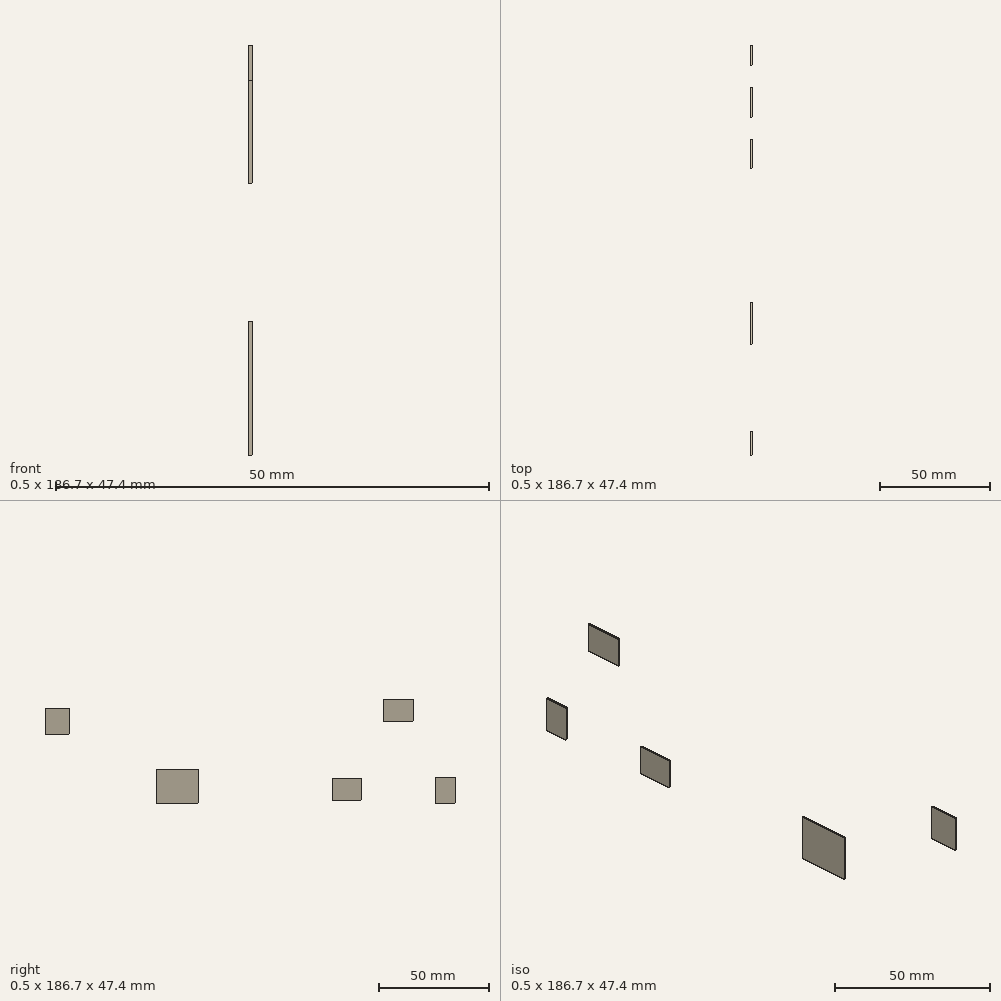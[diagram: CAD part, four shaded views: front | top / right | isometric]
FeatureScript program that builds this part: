
annotation { "Feature Type Name" : "Feature", "Feature Type Description" : "" }
export const myFeature = defineFeature(function(context is Context, id is Id, definition is map)
    precondition{}
    {
        {
            var Q0;
            Q0=qCreatedBy(makeId("Right.planeOp"),FACE);
            var sketch = newSketch(context, id + "F0", { "sketchPlane" : qUnion([Q0])});
            skLineSegment(sketch, "E0", {"start": v(-91.22, 37.12) * mm, "end": v(-91.22, 21.62) * mm});
            skLineSegment(sketch, "E1", {"start": v(-91.22, 37.12) * mm, "end": v(-110.22, 37.12) * mm});
            skLineSegment(sketch, "E2", {"start": v(-91.22, 21.62) * mm, "end": v(-110.22, 21.62) * mm});
            skLineSegment(sketch, "E3", {"start": v(-110.22, 21.62) * mm, "end": v(-110.22, 37.12) * mm});
            skLineSegment(sketch, "E4", {"start": v(-160.87, 65.02) * mm, "end": v(-149.87, 65.02) * mm});
            skLineSegment(sketch, "E5", {"start": v(-149.87, 65.02) * mm, "end": v(-149.87, 53.02) * mm});
            skLineSegment(sketch, "E6", {"start": v(-149.87, 53.02) * mm, "end": v(-160.87, 53.02) * mm});
            skLineSegment(sketch, "E7", {"start": v(-160.87, 53.02) * mm, "end": v(-160.87, 65.02) * mm});
            skLineSegment(sketch, "E8", {"start": v(-7.22, 69.02) * mm, "end": v(-7.22, 59.02) * mm});
            skLineSegment(sketch, "E9", {"start": v(-7.22, 59.02) * mm, "end": v(6.78, 59.02) * mm});
            skLineSegment(sketch, "E10", {"start": v(6.78, 59.02) * mm, "end": v(6.78, 69.02) * mm});
            skLineSegment(sketch, "E11", {"start": v(6.78, 69.02) * mm, "end": v(-7.22, 69.02) * mm});
            skLineSegment(sketch, "E12", {"start": v(-30.22, 33.12) * mm, "end": v(-17.22, 33.12) * mm});
            skLineSegment(sketch, "E13", {"start": v(-17.22, 23.12) * mm, "end": v(-30.22, 23.12) * mm});
            skLineSegment(sketch, "E14", {"start": v(-30.22, 23.12) * mm, "end": v(-30.22, 33.12) * mm});
            skLineSegment(sketch, "E15", {"start": v(25.78, 21.62) * mm, "end": v(25.78, 33.12) * mm});
            skLineSegment(sketch, "E16", {"start": v(16.78, 33.12) * mm, "end": v(16.78, 23.12) * mm});
            skLineSegment(sketch, "E17", {"start": v(25.78, 33.62) * mm, "end": v(16.35, 33.62) * mm});
            skLineSegment(sketch, "E18", {"start": v(25.78, 21.62) * mm, "end": v(16.78, 21.62) * mm});
            skLineSegment(sketch, "E19", {"start": v(-17.22, 33.12) * mm, "end": v(-17.22, 23.12) * mm});
            skLineSegment(sketch, "E20", {"start": v(16.78, 23.12) * mm, "end": v(16.78, 21.62) * mm});
            skLineSegment(sketch, "E21", {"start": v(16.78, 33.12) * mm, "end": v(16.78, 33.62) * mm});
            skLineSegment(sketch, "E22", {"start": v(25.78, 33.62) * mm, "end": v(25.78, 33.12) * mm});
            skPoint(sketch, "E23.end.orphan", {"position": v(25.78, 42.02) * mm});
            skSolve(sketch);
        }
        {
            var Q0;
            Q0=makeQuery(id+"F0.imprint","IMPRINT",FACE,{"disambiguationData":[TD([[makeQuery(id+"F0.imprint","IMPRINT",EDGE,{"derivedFrom":sQuery(id+"F0.wireOp",EDGE,"E4")}),-1.0]])]});
            var Q1;
            Q1=makeQuery(id+"F0.imprint","IMPRINT",FACE,{"disambiguationData":[TD([[makeQuery(id+"F0.imprint","IMPRINT",EDGE,{"derivedFrom":sQuery(id+"F0.wireOp",EDGE,"E0")}),-1.0]])]});
            var Q2;
            Q2=makeQuery(id+"F0.imprint","IMPRINT",FACE,{"disambiguationData":[TD([[makeQuery(id+"F0.imprint","IMPRINT",EDGE,{"derivedFrom":sQuery(id+"F0.wireOp",EDGE,"E12")}),-1.0]])]});
            var Q3;
            Q3=makeQuery(id+"F0.imprint","IMPRINT",FACE,{"disambiguationData":[TD([[makeQuery(id+"F0.imprint","IMPRINT",EDGE,{"derivedFrom":sQuery(id+"F0.wireOp",EDGE,"E15")}),1.0]])]});
            var Q4;
            Q4=makeQuery(id+"F0.imprint","IMPRINT",FACE,{"disambiguationData":[TD([[makeQuery(id+"F0.imprint","IMPRINT",EDGE,{"derivedFrom":sQuery(id+"F0.wireOp",EDGE,"E8")}),1.0]])]});
            extrude(context, id + "F1", {"entities" : qUnion([Q0, Q1, Q2, Q3, Q4]), "depth" : .5 * mm, "offsetDistance" : 25 * mm});
        }
    });
